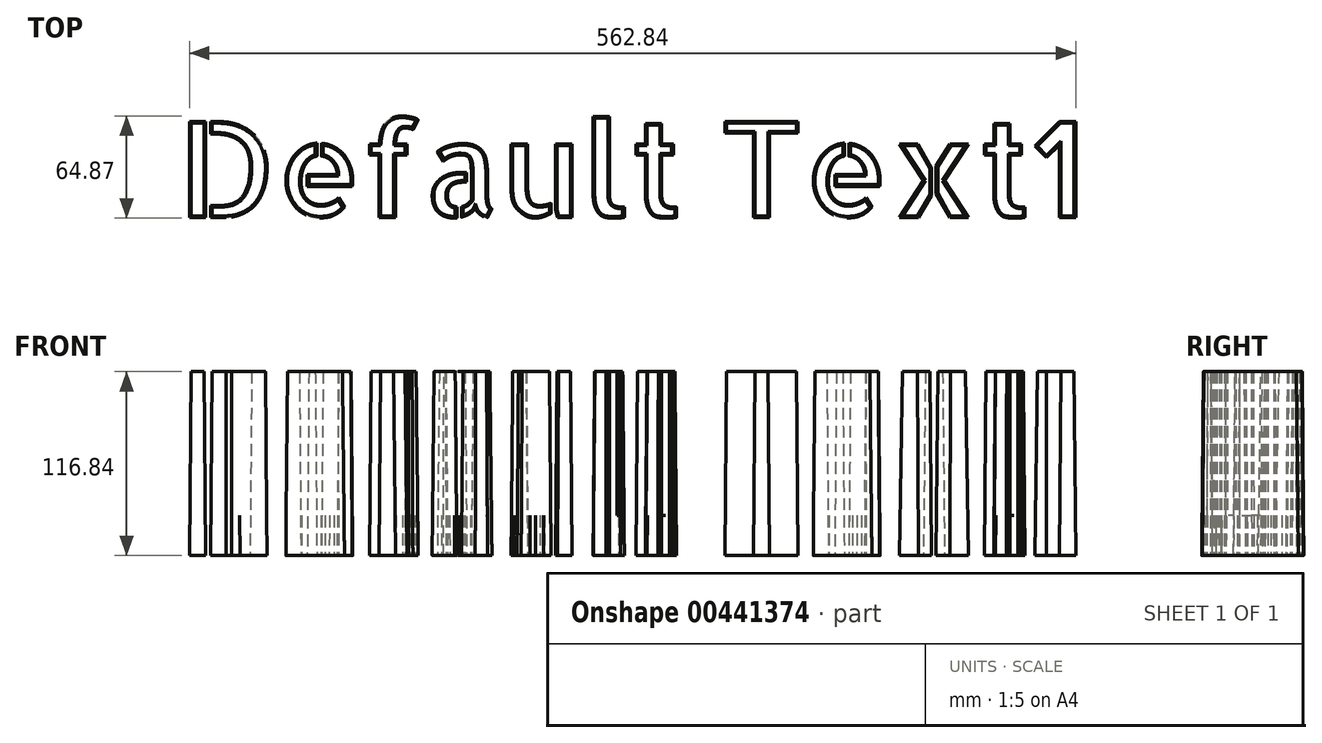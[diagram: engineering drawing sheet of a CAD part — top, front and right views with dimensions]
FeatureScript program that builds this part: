
annotation { "Feature Type Name" : "Feature", "Feature Type Description" : "" }
export const myFeature = defineFeature(function(context is Context, id is Id, definition is map)
    precondition{}
    {
        {
            var Q0;
            Q0=qCreatedBy(makeId("Top.planeOp"),FACE);
            var sketch = newSketch(context, id + "F0", { "sketchPlane" : qUnion([Q0])});
            skText(sketch, "E0", { "text": "Default Text1", "fontName": "AllertaStencil-Regular.ttf"});
            const initialGuessF0  = {"E0": [-0.05838, -0.07913, 1, 0, 0.06044]};
            skSetInitialGuess(sketch, initialGuessF0);
            skSolve(sketch);
        }
        {
            var Q0;
            Q0 = qSketchRegion(id + "F0", true);
            extrude(context, id + "F1", {"entities" : qUnion([Q0]), "depth" : 91.44 * mm, "hasDraft" : true, "draftAngle" : .5 * degree, "draftPullDirection" : true, "hasSecondDirection" : true, "secondDirectionOppositeDirection" : true, "secondDirectionDepth" : 25.4 * mm, "hasSecondDirectionDraft" : true, "secondDirectionDraftAngle" : 0.5 * degree});
        }
    });
